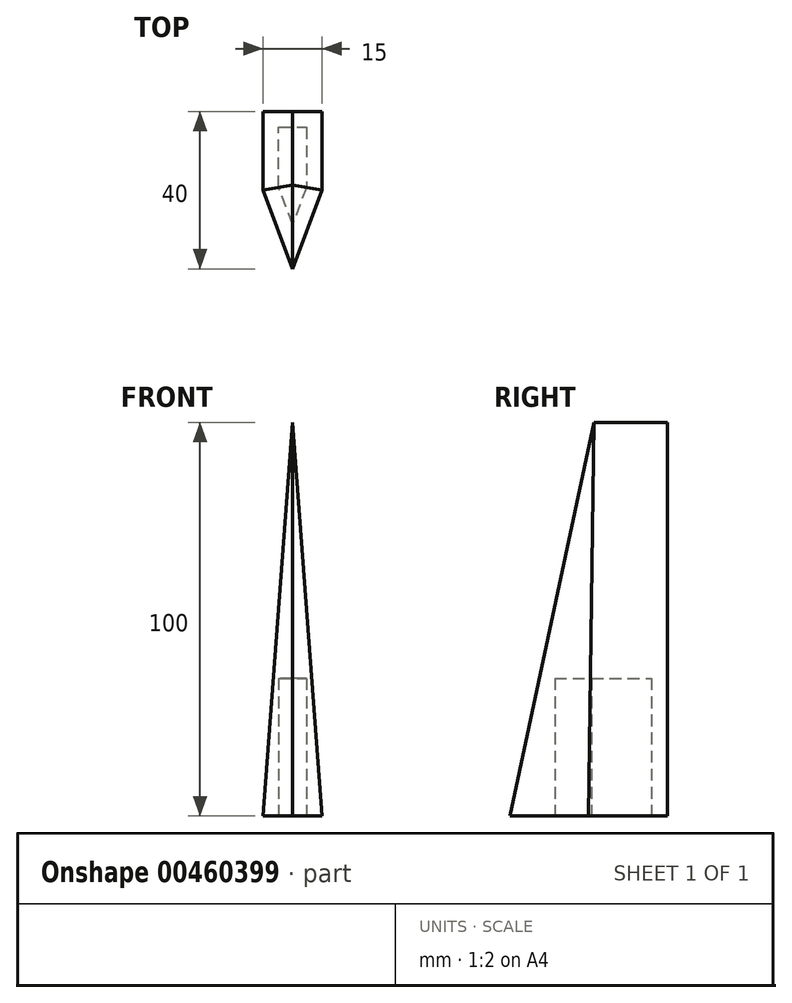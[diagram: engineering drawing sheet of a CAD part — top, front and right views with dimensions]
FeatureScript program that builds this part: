
annotation { "Feature Type Name" : "Feature", "Feature Type Description" : "" }
export const myFeature = defineFeature(function(context is Context, id is Id, definition is map)
    precondition{}
    {
        {
            var Q0;
            Q0=qCreatedBy(makeId("Top.planeOp"),FACE);
            var sketch = newSketch(context, id + "F0", { "sketchPlane" : qUnion([Q0])});
            skLineSegment(sketch, "E0", {"start": v(-7.5, 0) * mm, "end": v(-7.5, 20) * mm});
            skLineSegment(sketch, "E1", {"start": v(-7.5, 20) * mm, "end": v(7.5, 20) * mm});
            skLineSegment(sketch, "E2", {"start": v(7.5, 20) * mm, "end": v(7.5, 0) * mm});
            skLineSegment(sketch, "E3", {"start": v(7.5, 0) * mm, "end": v(0, -20) * mm});
            skLineSegment(sketch, "E4", {"start": v(0, -20) * mm, "end": v(-7.5, 0) * mm});
            skLineSegment(sketch, "E5", {"start": v(0, -20) * mm, "end": v(0, 20) * mm, "construction": true});
            skSolve(sketch);
        }
        {
            var Q0;
            Q0=makeQuery(id+"F0.imprint","IMPRINT",FACE,{"disambiguationData":[TD([[makeQuery(id+"F0.imprint","IMPRINT",EDGE,{"derivedFrom":sQuery(id+"F0.wireOp",EDGE,"E0")}),-1.0]])]});
            extrude(context, id + "F1", {"entities" : qUnion([Q0]), "depth" : 100 * mm});
        }
        {
            var Q0;
            Q0=makeQuery(id+"F1.opExtrude","CAP_FACE",FACE,{"disambiguationData":[OSD([sQuery(id+"F0.wireOp",EDGE,"E0"),sQuery(id+"F0.wireOp",EDGE,"E1"),sQuery(id+"F0.wireOp",EDGE,"E2"),sQuery(id+"F0.wireOp",EDGE,"E3"),sQuery(id+"F0.wireOp",EDGE,"E4")])],"isStart":true});
            var sketch = newSketch(context, id + "F2", { "sketchPlane" : qUnion([Q0])});
            skLineSegment(sketch, "E6.0", {"start": v(-3.5, -0.73) * mm, "end": v(-3.5, -16) * mm});
            skLineSegment(sketch, "E6.1", {"start": v(0, 8.6) * mm, "end": v(-3.5, -0.73) * mm});
            skLineSegment(sketch, "E6.2", {"start": v(-3.5, -16) * mm, "end": v(3.5, -16) * mm});
            skLineSegment(sketch, "E6.3", {"start": v(3.5, -16) * mm, "end": v(3.5, -0.73) * mm});
            skLineSegment(sketch, "E6.4", {"start": v(3.5, -0.73) * mm, "end": v(0, 8.6) * mm});
            skSolve(sketch);
        }
        {
            var Q0;
            Q0=qSketchRegion(id+"F2",true);
            extrude(context, id + "F3", {"entities" : qUnion([Q0]), "operationType" : NewBodyOperationType.REMOVE, "oppositeDirection" : true, "depth" : 35 * mm, "offsetDistance" : 25 * mm});
        }
        {
            var Q0;
            Q0=makeQuery(id+"F1.opExtrude","CAP_EDGE",EDGE,{"disambiguationData":[OSD([sQuery(id+"F0.wireOp",EDGE,"E3")])],"isStart":false});
            var Q1;
            Q1=makeQuery(id+"F1.opExtrude","CAP_EDGE",EDGE,{"disambiguationData":[OSD([sQuery(id+"F0.wireOp",EDGE,"E4")])],"isStart":false});
            var Q2;
            Q2=makeQuery(id+"F1.opExtrude","CAP_EDGE",EDGE,{"disambiguationData":[OSD([sQuery(id+"F0.wireOp",EDGE,"E2")])],"isStart":false});
            var Q3;
            Q3=makeQuery(id+"F1.opExtrude","CAP_EDGE",EDGE,{"disambiguationData":[OSD([sQuery(id+"F0.wireOp",EDGE,"E0")])],"isStart":false});
            chamfer(context, id + "F4", {"entities" : qUnion([Q0, Q1, Q2, Q3]), "chamferType" : ChamferType.TWO_OFFSETS, "width1" : 100 * mm, "oppositeDirection" : false, "width2" : 7.5 * mm, "tangentPropagation" : true});
        }
    });
